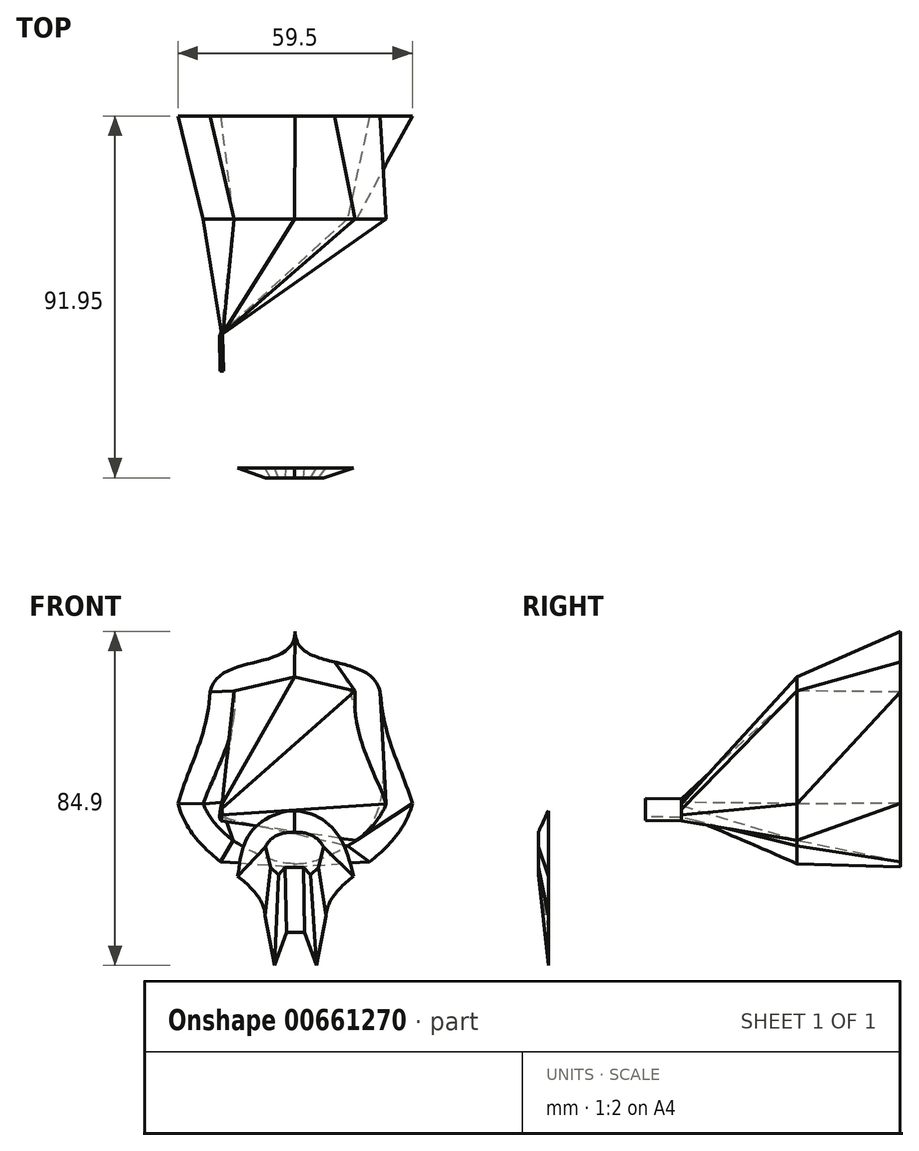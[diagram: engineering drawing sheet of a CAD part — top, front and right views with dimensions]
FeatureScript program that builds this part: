
annotation { "Feature Type Name" : "Feature", "Feature Type Description" : "" }
export const myFeature = defineFeature(function(context is Context, id is Id, definition is map)
    precondition{}
    {
        {
            var Q0;
            Q0=qCreatedBy(makeId("Front.planeOp"),FACE);
            cPlane(context, id + "F0", {"entities" : qUnion([Q0]), "cplaneType" : CPlaneType.OFFSET, "offset" : 32.5 * mm, "width" : 152.4 * mm, "height" : 152.4 * mm});
        }
        {
            var Q0;
            Q0=qCreatedBy(makeId("Front.planeOp"),FACE);
            cPlane(context, id + "F1", {"entities" : qUnion([Q0]), "cplaneType" : CPlaneType.OFFSET, "offset" : 43.94 * mm, "oppositeDirection" : true, "width" : 152.4 * mm, "height" : 152.4 * mm});
        }
        {
            var Q0;
            Q0=qCreatedBy(makeId("Front.planeOp"),FACE);
            cPlane(context, id + "F2", {"entities" : qUnion([Q0]), "cplaneType" : CPlaneType.OFFSET, "offset" : 26.16 * mm, "oppositeDirection" : true, "width" : 152.4 * mm, "height" : 152.4 * mm});
        }
        {
            var Q0;
            Q0=qCreatedBy(id+"F2.planeOp",FACE);
            var sketch = newSketch(context, id + "F3", { "sketchPlane" : qUnion([Q0])});
            skFitSpline(sketch, "E0", {"points": [v(-20.95, 65.73) * mm, v(-42.56, 50.3) * mm], "startDerivative": vector(0, -31.5) * mm, "endDerivative": vector(-6.43, -30.85) * mm});
            skFitSpline(sketch, "E1", {"points": [v(-50.7, 21.98) * mm, v(-28.66, -6.31) * mm], "startDerivative": vector(11, -44.36) * mm, "endDerivative": vector(2.16, -30.8) * mm});
            skFitSpline(sketch, "E2.MirrorCS", {"points": [v(-20.95, 65.73) * mm, v(0.66, 50.3) * mm], "startDerivative": vector(0, -31.5) * mm, "endDerivative": vector(6.43, -30.85) * mm});
            skFitSpline(sketch, "E3.MirrorCS", {"points": [v(8.8, 21.98) * mm, v(-13.24, -6.31) * mm], "startDerivative": vector(-11, -44.36) * mm, "endDerivative": vector(-2.16, -30.8) * mm});
            skFitSpline(sketch, "E4", {"points": [v(-42.56, 50.3) * mm, v(-50.7, 21.98) * mm], "startDerivative": vector(-1.35, -31.72) * mm, "endDerivative": vector(-8.14, -28.33) * mm});
            skFitSpline(sketch, "E5", {"points": [v(0.66, 50.3) * mm, v(8.8, 21.98) * mm], "startDerivative": vector(3.42, -39.6) * mm, "endDerivative": vector(8.14, -28.33) * mm});
            skLineSegment(sketch, "E6", {"start": v(-39.9, 7.2) * mm, "end": v(-20.95, 5.91) * mm});
            skLineSegment(sketch, "E7", {"start": v(-20.95, 5.91) * mm, "end": v(-2, 7.2) * mm});
            skSolve(sketch);
        }
        {
            var Q0;
            Q0=qCreatedBy(makeId("Front.planeOp"),FACE);
            var sketch = newSketch(context, id + "F4", { "sketchPlane" : qUnion([Q0])});
            skFitSpline(sketch, "E8.0", {"points": [v(-36.42, 12.51) * mm, v(-34.56, 11.3) * mm, v(-31.12, 9.33) * mm, v(-26.76, 7.58) * mm, v(-23.07, 6.8) * mm, v(-19.8, 6.73) * mm, v(-16.6, 7.27) * mm, v(-13.2, 8.43) * mm, v(-9.46, 10.21) * mm, v(-6.7, 11.79) * mm, v(-5.26, 12.65) * mm]});
            skFitSpline(sketch, "E9.0", {"points": [v(2.63, 23.5) * mm, v(2.47, 22.86) * mm, v(2.08, 21.64) * mm, v(1.3, 19.98) * mm, v(0.3, 18.4) * mm, v(-1.27, 16.39) * mm, v(-3.73, 13.97) * mm, v(-7.23, 11.13) * mm, v(-10.38, 8.68) * mm, v(-12.88, 6.5) * mm, v(-14.7, 4.7) * mm, v(-16.44, 2.62) * mm, v(-17.96, 0.19) * mm, v(-19.12, -2.66) * mm, v(-19.5, -4.78) * mm, v(-19.58, -5.87) * mm]});
            skFitSpline(sketch, "E10.0", {"points": [v(-5.68, 50.69) * mm, v(-5.78, 48.99) * mm, v(-5.73, 45.7) * mm, v(-5.01, 41.14) * mm, v(-3.86, 36.97) * mm, v(-2.46, 33.15) * mm, v(-0.97, 29.63) * mm, v(0.47, 26.33) * mm, v(1.74, 23.21) * mm, v(2.41, 21.22) * mm, v(2.7, 20.23) * mm]});
            skPoint(sketch, "E11", {"position": v(-21.05, 54.2) * mm});
            skLineSegment(sketch, "E12", {"start": v(-21.05, 54.2) * mm, "end": v(-5.69, 50.62) * mm});
            skLineSegment(sketch, "E13.MirrorCS", {"start": v(-21.05, 54.2) * mm, "end": v(-36.42, 50.62) * mm});
            skFitSpline(sketch, "E14.MirrorCS", {"points": [v(-36.42, 50.69) * mm, v(-36.32, 48.99) * mm, v(-36.38, 45.7) * mm, v(-37.1, 41.14) * mm, v(-38.24, 36.97) * mm, v(-39.65, 33.15) * mm, v(-41.14, 29.63) * mm, v(-42.57, 26.33) * mm, v(-43.84, 23.21) * mm, v(-44.52, 21.22) * mm, v(-44.8, 20.23) * mm]});
            skFitSpline(sketch, "E15.MirrorCS", {"points": [v(-44.74, 23.5) * mm, v(-44.58, 22.86) * mm, v(-44.19, 21.64) * mm, v(-43.4, 19.98) * mm, v(-42.41, 18.4) * mm, v(-40.83, 16.39) * mm, v(-38.38, 13.97) * mm, v(-34.87, 11.13) * mm, v(-31.73, 8.68) * mm, v(-29.23, 6.5) * mm, v(-27.4, 4.7) * mm, v(-25.67, 2.62) * mm, v(-24.14, 0.19) * mm, v(-22.99, -2.66) * mm, v(-22.6, -4.78) * mm, v(-22.53, -5.87) * mm]});
            skFitSpline(sketch, "E16.MirrorCS", {"points": [v(-5.68, 12.51) * mm, v(-7.54, 11.3) * mm, v(-10.98, 9.33) * mm, v(-15.35, 7.58) * mm, v(-19.04, 6.8) * mm, v(-22.3, 6.73) * mm, v(-25.5, 7.27) * mm, v(-28.9, 8.43) * mm, v(-32.65, 10.21) * mm, v(-35.4, 11.79) * mm, v(-36.84, 12.65) * mm]});
            skPoint(sketch, "E17.orphan", {"position": v(-21.05, 65.79) * mm});
            skSolve(sketch);
        }
        {
            var Q0;
            Q0=qCreatedBy(makeId("Front.planeOp"),FACE);
            cPlane(context, id + "F5", {"entities" : qUnion([Q0]), "cplaneType" : CPlaneType.OFFSET, "offset" : 63.25 * mm, "width" : 152.4 * mm, "height" : 152.4 * mm});
        }
        {
            var Q0;
            Q0=qCreatedBy(id+"F0.planeOp",FACE);
            cPlane(context, id + "F6", {"entities" : qUnion([Q0]), "cplaneType" : CPlaneType.OFFSET, "offset" : 6.1 * mm, "width" : 152.4 * mm, "height" : 152.4 * mm});
        }
        {
            var Q0;
            Q0=qCreatedBy(id+"F0.planeOp",FACE);
            cPlane(context, id + "F7", {"entities" : qUnion([Q0]), "cplaneType" : CPlaneType.OFFSET, "offset" : 3.05 * mm, "oppositeDirection" : true, "width" : 152.4 * mm, "height" : 152.4 * mm});
        }
        {
            var Q0;
            Q0=qCreatedBy(id+"F7.planeOp",FACE);
            var sketch = newSketch(context, id + "F8", { "sketchPlane" : qUnion([Q0])});
            skPoint(sketch, "E18.MirrorCS.end.orphan", {"position": v(-1.17, 23.82) * mm});
            skPoint(sketch, "E18.MirrorCS.start.orphan", {"position": v(-9.87, 34.35) * mm});
            skFitSpline(sketch, "E19", {"points": [v(-40.17, 18.5) * mm, v(-28.92, 10.6) * mm], "startDerivative": vector(8.05, -20.25) * mm, "endDerivative": vector(16.84, 1.77) * mm});
            skPoint(sketch, "E20", {"position": v(-20.56, 33.83) * mm});
            skPoint(sketch, "E21", {"position": v(-31, 32.27) * mm});
            skPoint(sketch, "E22", {"position": v(-10.87, 32.4) * mm});
            skFitSpline(sketch, "E23.trimOffspring", {"points": [v(-2.25, 7.06) * mm, v(-2.25, 24.88) * mm, v(-10.87, 32.4) * mm, v(-31, 32.27) * mm, v(-39.15, 23.82) * mm, v(-40.13, 7.06) * mm], "startDerivative": vector(11.5, 92.94) * mm, "endDerivative": vector(3.84, -85.62) * mm});
            skLineSegment(sketch, "E24", {"start": v(-31, 32.27) * mm, "end": v(-20.56, 33.83) * mm});
            skFitSpline(sketch, "E25", {"points": [v(-28.92, 10.6) * mm, v(-20.56, 9.87) * mm], "startDerivative": vector(9.1, 2.28) * mm, "endDerivative": vector(8.33, -0.74) * mm});
            skLineSegment(sketch, "E26.MirrorCS", {"start": v(-10.12, 32.27) * mm, "end": v(-20.56, 33.83) * mm});
            skFitSpline(sketch, "E27.MirrorCS", {"points": [v(-38.87, 7.06) * mm, v(-38.87, 24.88) * mm, v(-30.25, 32.4) * mm, v(-10.12, 32.27) * mm, v(-1.97, 23.82) * mm, v(-0.99, 7.06) * mm], "startDerivative": vector(-11.5, 92.94) * mm, "endDerivative": vector(-3.84, -85.62) * mm});
            skFitSpline(sketch, "E28.MirrorCS", {"points": [v(-0.95, 18.5) * mm, v(-12.2, 10.6) * mm], "startDerivative": vector(-8.05, -20.25) * mm, "endDerivative": vector(-16.84, 1.77) * mm});
            skFitSpline(sketch, "E29.MirrorCS", {"points": [v(-12.2, 10.6) * mm, v(-20.56, 9.87) * mm], "startDerivative": vector(-9.1, 2.28) * mm, "endDerivative": vector(-8.33, -0.74) * mm});
            skSolve(sketch);
        }
        {
            var Q0;
            Q0=qCreatedBy(id+"F5.planeOp",FACE);
            var sketch = newSketch(context, id + "F9", { "sketchPlane" : qUnion([Q0])});
            skLineSegment(sketch, "E30", {"start": v(-28.55, -6.57) * mm, "end": v(-26.2, -19.36) * mm});
            skLineSegment(sketch, "E31", {"start": v(-26.2, -19.36) * mm, "end": v(-23.14, -10.72) * mm});
            skLineSegment(sketch, "E32", {"start": v(-13.13, -6.57) * mm, "end": v(-15.58, -19.36) * mm});
            skLineSegment(sketch, "E33", {"start": v(-15.58, -19.36) * mm, "end": v(-18.53, -10.72) * mm});
            skLineSegment(sketch, "E34.MirrorCS", {"start": v(-3.58, -6.57) * mm, "end": v(-6.15, 3.54) * mm});
            skLineSegment(sketch, "E35.MirrorCS", {"start": v(-28.55, -6.57) * mm, "end": v(-26.1, -19.36) * mm});
            skLineSegment(sketch, "E36.MirrorCS", {"start": v(-26.1, -19.36) * mm, "end": v(-23.14, -10.72) * mm});
            skLineSegment(sketch, "E37.MirrorCS", {"start": v(-15.47, -19.36) * mm, "end": v(-18.53, -10.72) * mm});
            skFitSpline(sketch, "E38.trimOffspring", {"points": [v(-50.59, 21.73) * mm, v(-28.55, -6.57) * mm], "startDerivative": vector(11, -44.36) * mm, "endDerivative": vector(2.16, -30.8) * mm});
            skFitSpline(sketch, "E39.trimOffspring", {"points": [v(8.91, 21.73) * mm, v(-13.13, -6.57) * mm], "startDerivative": vector(-11, -44.36) * mm, "endDerivative": vector(-2.16, -30.8) * mm});
            skPoint(sketch, "E40.start.orphan", {"position": v(-39.78, 6.94) * mm});
            skPoint(sketch, "E41.start.orphan", {"position": v(-38.1, -6.57) * mm});
            skFitSpline(sketch, "E42", {"points": [v(-6.15, 3.54) * mm, v(-10.6, 14.77) * mm, v(-21.07, 20.12) * mm, v(-32.12, 14.77) * mm, v(-35.52, 3.54) * mm], "startDerivative": vector(-11.75, 48.33) * mm, "endDerivative": vector(-6.14, -49.15) * mm});
            skLineSegment(sketch, "E43", {"start": v(-23.14, -10.72) * mm, "end": v(-18.53, -10.72) * mm});
            skSolve(sketch);
        }
        {
            var Q0;
            Q0=qCreatedBy(id+"F6.planeOp",FACE);
            cPlane(context, id + "F10", {"entities" : qUnion([Q0]), "cplaneType" : CPlaneType.OFFSET, "offset" : 19.05 * mm, "width" : 152.4 * mm, "height" : 152.4 * mm});
        }
        {
            var Q0;
            Q0=makeQuery(id+"F4.imprint","IMPRINT",FACE,{"disambiguationData":[TD([[makeQuery(id+"F4.imprint","IMPRINT",EDGE,{"derivedFrom":sQuery(id+"F4.wireOp",EDGE,"E8.0")}),1.0]])]});
            var Q1;
            Q1=makeQuery(id+"F8.imprint","IMPRINT",FACE,{"disambiguationData":[TD([[makeQuery(id+"F8.imprint","IMPRINT",EDGE,{"derivedFrom":sQuery(id+"F8.wireOp",EDGE,"E19")}),1.0]])]});
            loft(context, id + "F11", {"sheetProfilesArray" : [{ "sheetProfileEntities" : qUnion([Q0]) }, { "sheetProfileEntities" : qUnion([Q1]) }]});
        }
        {
            var Q1;
            {var subQ1=sQuery(id+"F3.wireOp",EDGE,"E0");Q1=makeQuery(id+"F3.imprint","IMPRINT",FACE,{"disambiguationData":[TD([[makeQuery(id+"F3.imprint","IMPRINT",EDGE,{"derivedFrom":subQ1}),1.0]])]});}
            var Q2;
            Q2=makeQuery(id+"F11.opLoft","CAP_FACE",FACE,{"disambiguationData":[OSD([makeQuery(id+"F4.imprint","IMPRINT",FACE,{"disambiguationData":[TD([[makeQuery(id+"F4.imprint","IMPRINT",EDGE,{"derivedFrom":sQuery(id+"F4.wireOp",EDGE,"E8.0")}),1.0]])]})])],"isStart":true});
            loft(context, id + "F12", {"operationType" : NewBodyOperationType.ADD, "sheetProfilesArray" : [{ "sheetProfileEntities" : qUnion([Q1]) }, { "sheetProfileEntities" : qUnion([Q2]) }]});
        }
        {
            var Q0;
            Q0=qCreatedBy(id+"F5.planeOp",FACE);
            cPlane(context, id + "F13", {"entities" : qUnion([Q0]), "cplaneType" : CPlaneType.OFFSET, "offset" : 2.54 * mm, "width" : 152.4 * mm, "height" : 152.4 * mm});
        }
        {
            var Q0;
            Q0=qCreatedBy(id+"F13.planeOp",FACE);
            var sketch = newSketch(context, id + "F14", { "sketchPlane" : qUnion([Q0])});
            skFitSpline(sketch, "E44", {"points": [v(-28.53, 10.93) * mm, v(-21.15, 14.55) * mm], "startDerivative": vector(4.1, 8.58) * mm, "endDerivative": vector(8.8, -1.32) * mm});
            skLineSegment(sketch, "E45", {"start": v(-28.53, 10.93) * mm, "end": v(-27.26, 5.78) * mm});
            skLineSegment(sketch, "E46", {"start": v(-27.26, 5.78) * mm, "end": v(-25.22, 3.91) * mm});
            skLineSegment(sketch, "E47", {"start": v(-25.22, 3.91) * mm, "end": v(-23.5, 5.78) * mm});
            skFitSpline(sketch, "E48.MirrorCS", {"points": [v(-13.76, 10.93) * mm, v(-21.15, 14.55) * mm], "startDerivative": vector(-4.1, 8.58) * mm, "endDerivative": vector(-8.8, -1.32) * mm});
            skLineSegment(sketch, "E49.MirrorCS", {"start": v(-13.76, 10.93) * mm, "end": v(-15.04, 5.78) * mm});
            skLineSegment(sketch, "E50.MirrorCS", {"start": v(-17.07, 3.91) * mm, "end": v(-18.79, 5.78) * mm});
            skLineSegment(sketch, "E51.MirrorCS", {"start": v(-15.04, 5.78) * mm, "end": v(-17.07, 3.91) * mm});
            skLineSegment(sketch, "E52", {"start": v(-23.5, 5.78) * mm, "end": v(-18.79, 5.78) * mm});
            skSolve(sketch);
        }
        {
            var Q0;
            Q0=makeQuery(id+"F14.imprint","IMPRINT",FACE,{"disambiguationData":[TD([[makeQuery(id+"F14.imprint","IMPRINT",EDGE,{"derivedFrom":sQuery(id+"F14.wireOp",EDGE,"E44")}),-1.0]])]});
            var Q1;
            {var subQ4=sQuery(id+"F9.wireOp",EDGE,"E38.trimOffspring");Q1=makeQuery(id+"F9.imprint","IMPRINT",FACE,{"disambiguationData":[TD([[makeQuery(id+"F9.imprint","IMPRINT",EDGE,{"derivedFrom":subQ4}),1.0]])]});}
            loft(context, id + "F15", {"sheetProfilesArray" : [{ "sheetProfileEntities" : qUnion([Q0]) }, { "sheetProfileEntities" : qUnion([Q1]) }]});
        }
        {
            var Q0;
            Q0=qCreatedBy(id+"F6.planeOp",FACE);
            var sketch = newSketch(context, id + "F16", { "sketchPlane" : qUnion([Q0])});
            skPoint(sketch, "E53.MirrorCS.end.orphan", {"position": v(-0.97, 23.9) * mm});
            skPoint(sketch, "E53.MirrorCS.start.orphan", {"position": v(-9.67, 34.43) * mm});
            skFitSpline(sketch, "E54", {"points": [v(-39.97, 18.58) * mm, v(-28.72, 10.68) * mm], "startDerivative": vector(8.05, -20.25) * mm, "endDerivative": vector(16.84, 1.77) * mm});
            skPoint(sketch, "E55", {"position": v(-20.36, 33.9) * mm});
            skPoint(sketch, "E56", {"position": v(-30.8, 32.35) * mm});
            skPoint(sketch, "E57", {"position": v(-10.67, 32.48) * mm});
            skFitSpline(sketch, "E58.trimOffspring", {"points": [v(-2.05, 7.14) * mm, v(-2.05, 24.96) * mm, v(-10.67, 32.48) * mm, v(-30.8, 32.35) * mm, v(-38.95, 23.9) * mm, v(-39.93, 7.14) * mm], "startDerivative": vector(11.5, 92.94) * mm, "endDerivative": vector(3.84, -85.62) * mm});
            skLineSegment(sketch, "E59", {"start": v(-30.8, 32.35) * mm, "end": v(-20.36, 33.9) * mm});
            skFitSpline(sketch, "E60", {"points": [v(-28.72, 10.68) * mm, v(-20.36, 9.96) * mm], "startDerivative": vector(9.1, 2.28) * mm, "endDerivative": vector(8.33, -0.74) * mm});
            skLineSegment(sketch, "E61.MirrorCS", {"start": v(-9.92, 32.35) * mm, "end": v(-20.36, 33.9) * mm});
            skFitSpline(sketch, "E62.MirrorCS", {"points": [v(-38.67, 7.14) * mm, v(-38.67, 24.96) * mm, v(-30.05, 32.48) * mm, v(-9.92, 32.35) * mm, v(-1.77, 23.9) * mm, v(-0.78, 7.14) * mm], "startDerivative": vector(-11.5, 92.94) * mm, "endDerivative": vector(-3.84, -85.62) * mm});
            skFitSpline(sketch, "E63.MirrorCS", {"points": [v(-0.75, 18.58) * mm, v(-12, 10.68) * mm], "startDerivative": vector(-8.05, -20.25) * mm, "endDerivative": vector(-16.84, 1.77) * mm});
            skFitSpline(sketch, "E64.MirrorCS", {"points": [v(-12, 10.68) * mm, v(-20.36, 9.96) * mm], "startDerivative": vector(-9.1, 2.28) * mm, "endDerivative": vector(-8.33, -0.74) * mm});
            skSolve(sketch);
        }
        {
            var Q1;
            Q1=makeQuery(id+"F11.opLoft","CAP_FACE",FACE,{"disambiguationData":[OSD([makeQuery(id+"F8.imprint","IMPRINT",FACE,{"disambiguationData":[TD([[makeQuery(id+"F8.imprint","IMPRINT",EDGE,{"derivedFrom":sQuery(id+"F8.wireOp",EDGE,"E19")}),1.0]])]})])],"isStart":true});
            var Q2;
            Q2=makeQuery(id+"F16.imprint","IMPRINT",FACE,{"disambiguationData":[TD([[makeQuery(id+"F16.imprint","IMPRINT",EDGE,{"derivedFrom":sQuery(id+"F16.wireOp",EDGE,"E54")}),1.0]])]});
            loft(context, id + "F17", {"operationType" : NewBodyOperationType.ADD, "sheetProfilesArray" : [{ "sheetProfileEntities" : qUnion([Q1]) }, { "sheetProfileEntities" : qUnion([Q2]) }]});
        }
    });
